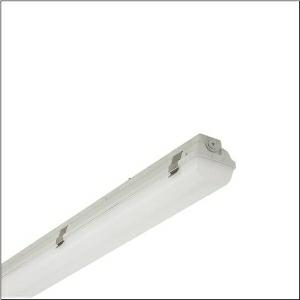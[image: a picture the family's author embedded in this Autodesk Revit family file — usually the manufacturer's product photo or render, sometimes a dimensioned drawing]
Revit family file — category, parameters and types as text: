
# Revit family: monsun_r__21_eco_51fj10mp47a_2b6f
name_source: partatom
category: Lighting Fixtures
units: mm (PartAtom-declared; Revit-internal decimal feet)

## family parameters
Cut with Voids When Loaded = No
Host = Face
Light Source = No
Part Type = Normal
Room Calculation Point = No
Round Connector Dimension = Use Diameter
Shared = No

## types (1)
- --- (1 x LED, 7000 lm, 50 W, 4000K)
    Apparent Load = 50 VA
    CIE Flux Codes = 41 70 89 90 100
    Color Rendering = 80
    Color Temperature = 4000K
    Default Elevation = 1800 mm
    Description = Monsun® 21 Eco, damp-proof luminaire, primary optical cover: diffuser, of PMMA, frosted, light emission: direct distribution, primary light characteristic: symmetric, installation type: suspended mounting, surface-mounted, LED, rated luminous flux: 7.000lm, luminous efficacy: 140lm/W, light colour: 840, colour temperature: 4000K, control gear: ON/OFF Multilumen, with terminal, 3-pole, max. 2.5mm², mains connection: 220..240V, AC, 50/60Hz, rated input power: 50W, housing, of glass-fibre reinforced polyester, light grey (RAL 7035), length: 1.577mm, width: 90mm, height: 95mm, clip for enclosure, of spring steel V2A, protection rating (complete): IP66, insulation class (complete): insulation class I (protective earthing), certification: CE, UKCA, protection symbol: D, impact resistance: IK02, permissible operating ambient temperature: -20..+35°C, corresponds to IFS (International Featured Standards) requirements for safety and quality in the food industry, contact your sales advisor before using the luminaires in applications with unclear chemical exposure, large temperature fluctuations or condensation-forming humidity, packaging unit: 1 piece
    Height = 103 mm
    Lamp = 1 x LED
    Lamp Light Flux = 7000 lm
    Lamp Power = 50 W
    Lamp count = 1
    Length = 1577 mm
    Luminous efficacy = 140 lm/W
    Manufacturer = Siteco
    ModVariant = No
    Model = 51FJ10MP47A
    Mounting Place = Ceiling
    Mounting Type = Surface mounted
    Number of Poles = 1
    OnlyDefault = Yes
    Power Factor = 1
    Product Name = Monsun® 21 Eco
    Product group = damp-proof luminaire
    ProductGroupID = 300
    Protection Class = Protection class I
    Protection Degree = IP 66
    RLX_Detail_Level = 1
    RLX_Emergency_Light_Flux = 0 lm
    RLX_Emergency_Type = 0
    RLX_Emergency_Type_DB = No
    RlxData = <blob elided: 34129 chars, md5=e053e8c5>
    Socket = socket
    Standby Power = 0 W
    System Light Flux = 7000 lm
    System Power = 50 W
    Type Comments = factory setting: luminous flux: 100 % | (ON | ON | ON | ON) | 350 mA
    Type Image = l_1007218.jpg
    URL = http://relux.com
    VarID = @adj_146202
    Voltage = 0 V
    Weight = 0.00 kg
    Width = 90 mm

## geometry (parser evidence)
native form markers: Blend x4, Sweep x13
no freeform markers — native parametric forms only
